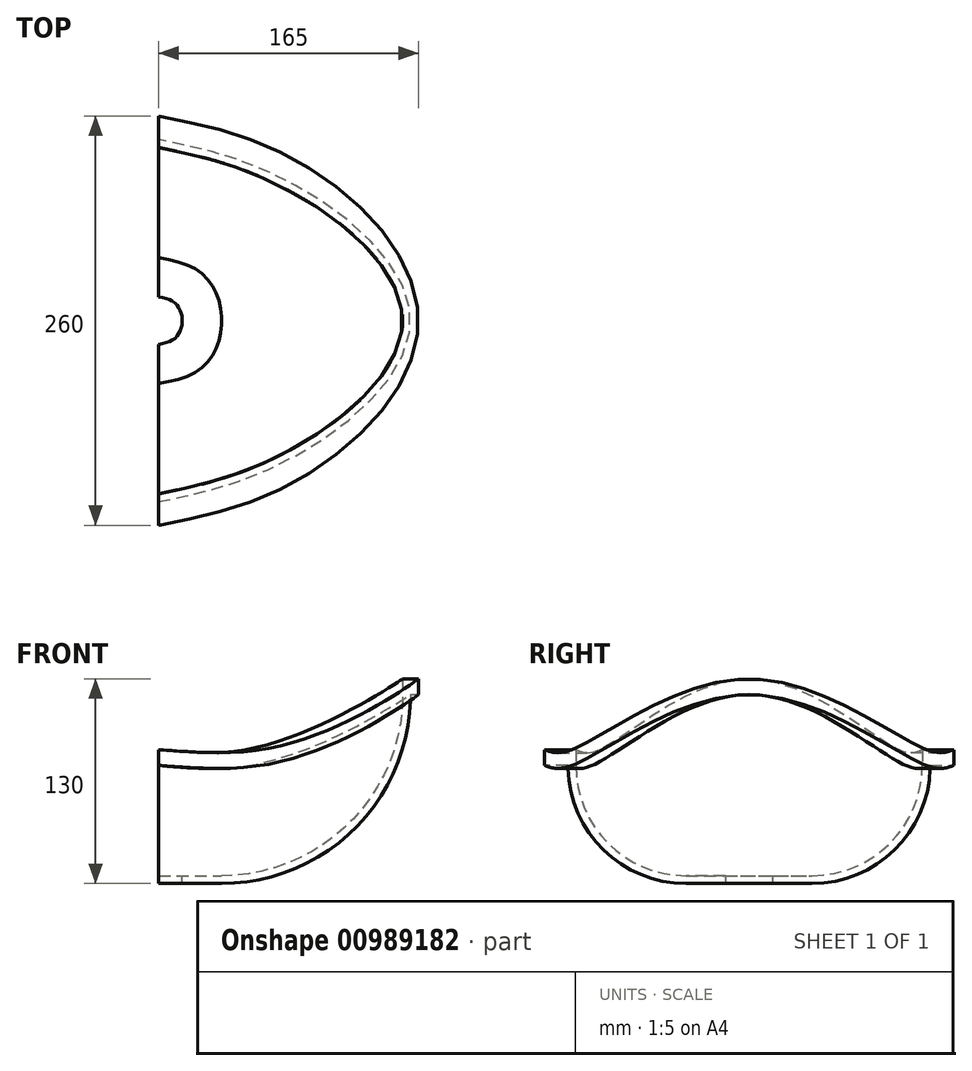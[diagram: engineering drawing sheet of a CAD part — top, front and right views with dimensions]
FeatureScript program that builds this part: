
annotation { "Feature Type Name" : "Feature", "Feature Type Description" : "" }
export const myFeature = defineFeature(function(context is Context, id is Id, definition is map)
    precondition{}
    {
        {
            var Q0;
            Q0=qCreatedBy(makeId("Front.planeOp"),FACE);
            var sketch = newSketch(context, id + "F0", { "sketchPlane" : qUnion([Q0])});
            skLineSegment(sketch, "E0.bottom", {"start": v(15, 5) * mm, "end": v(40, 5) * mm});
            skLineSegment(sketch, "E0.top", {"start": v(15, 0) * mm, "end": v(40, 0) * mm});
            skLineSegment(sketch, "E0.left", {"start": v(15, 5) * mm, "end": v(15, 0) * mm});
            skLineSegment(sketch, "E0.right", {"start": v(40, 5) * mm, "end": v(40, 0) * mm, "construction": true});
            skLineSegment(sketch, "E1.bottom", {"start": v(155, 130) * mm, "end": v(165, 130) * mm});
            skLineSegment(sketch, "E1.top", {"start": v(155, 120) * mm, "end": v(165, 120) * mm});
            skLineSegment(sketch, "E1.left", {"start": v(155, 130) * mm, "end": v(155, 120) * mm});
            skLineSegment(sketch, "E1.right", {"start": v(165, 130) * mm, "end": v(165, 120) * mm});
            skArc(sketch, "E2", {"start": v(40, 0) * mm, "mid": v(124.85, 35.15) * mm, "end": v(160, 120) * mm});
            skArc(sketch, "E3", {"start": v(40, 5) * mm, "mid": v(121.32, 38.68) * mm, "end": v(155, 120) * mm});
            skLineSegment(sketch, "E4", {"start": v(0, 0) * mm, "end": v(0, 10.01) * mm});
            skLineSegment(sketch, "E5", {"start": v(0, 0) * mm, "end": v(0, 50) * mm, "construction": true});
            skSolve(sketch);
        }
        {
            var Q0;
            Q0=sQuery(id+"F0.wireOp",EDGE,"E5");
            cPlane(context, id + "F1", {"entities" : qUnion([Q0]), "cplaneType" : CPlaneType.LINE_ANGLE, "offset" : 25 * mm, "angle" : 30 * degree, "oppositeDirection" : true, "width" : 150 * mm, "height" : 150 * mm});
        }
        {
            var Q0;
            Q0=qCreatedBy(id+"F1.planeOp",FACE);
            var sketch = newSketch(context, id + "F2", { "sketchPlane" : qUnion([Q0])});
            skLineSegment(sketch, "E6.bottom", {"start": v(15, 5) * mm, "end": v(40, 5) * mm});
            skLineSegment(sketch, "E6.top", {"start": v(15, 0) * mm, "end": v(40, 0) * mm});
            skLineSegment(sketch, "E6.left", {"start": v(15, 5) * mm, "end": v(15, 0) * mm});
            skLineSegment(sketch, "E6.right", {"start": v(40, 5) * mm, "end": v(40, 0) * mm, "construction": true});
            skLineSegment(sketch, "E7.bottom", {"start": v(110, 85) * mm, "end": v(130, 85) * mm});
            skLineSegment(sketch, "E7.top", {"start": v(110, 75) * mm, "end": v(130, 75) * mm});
            skLineSegment(sketch, "E7.left", {"start": v(110, 85) * mm, "end": v(110, 75) * mm});
            skLineSegment(sketch, "E7.right", {"start": v(130, 85) * mm, "end": v(130, 75) * mm});
            skArc(sketch, "E8", {"start": v(40, 0) * mm, "mid": v(93.03, 21.97) * mm, "end": v(115, 75) * mm});
            skArc(sketch, "E9", {"start": v(40, 5) * mm, "mid": v(89.5, 25.5) * mm, "end": v(110, 75) * mm});
            skLineSegment(sketch, "E10", {"start": v(0, 0) * mm, "end": v(0, 10.01) * mm});
            skLineSegment(sketch, "E11", {"start": v(0, 0) * mm, "end": v(0, 50) * mm, "construction": true});
            skSolve(sketch);
        }
        {
            var Q0;
            Q0=sQuery(id+"F0.wireOp",EDGE,"E5");
            cPlane(context, id + "F3", {"entities" : qUnion([Q0]), "cplaneType" : CPlaneType.LINE_ANGLE, "offset" : 25 * mm, "angle" : 150 * degree, "oppositeDirection" : true, "width" : 150 * mm, "height" : 150 * mm});
        }
        {
            var Q0;
            Q0=qCreatedBy(id+"F3.planeOp",FACE);
            var sketch = newSketch(context, id + "F4", { "sketchPlane" : qUnion([Q0])});
            skLineSegment(sketch, "E12.bottom", {"start": v(15, 5) * mm, "end": v(40, 5) * mm});
            skLineSegment(sketch, "E12.top", {"start": v(15, 0) * mm, "end": v(40, 0) * mm});
            skLineSegment(sketch, "E12.left", {"start": v(15, 5) * mm, "end": v(15, 0) * mm});
            skLineSegment(sketch, "E12.right", {"start": v(40, 5) * mm, "end": v(40, 0) * mm, "construction": true});
            skLineSegment(sketch, "E13.bottom", {"start": v(110, 85) * mm, "end": v(130, 85) * mm});
            skLineSegment(sketch, "E13.top", {"start": v(110, 75) * mm, "end": v(130, 75) * mm});
            skLineSegment(sketch, "E13.left", {"start": v(110, 85) * mm, "end": v(110, 75) * mm});
            skLineSegment(sketch, "E13.right", {"start": v(130, 85) * mm, "end": v(130, 75) * mm});
            skArc(sketch, "E14", {"start": v(40, 0) * mm, "mid": v(93.03, 21.97) * mm, "end": v(115, 75) * mm});
            skArc(sketch, "E15", {"start": v(40, 5) * mm, "mid": v(89.5, 25.5) * mm, "end": v(110, 75) * mm});
            skLineSegment(sketch, "E16", {"start": v(0, 0) * mm, "end": v(0, 10.01) * mm});
            skLineSegment(sketch, "E17", {"start": v(0, 0) * mm, "end": v(0, 50) * mm, "construction": true});
            skSolve(sketch);
        }
        {
            var Q0;
            Q0=qCreatedBy(makeId("Right.planeOp"),FACE);
            var sketch = newSketch(context, id + "F5", { "sketchPlane" : qUnion([Q0])});
            skLineSegment(sketch, "E18.bottom", {"start": v(15, 5) * mm, "end": v(40, 5) * mm});
            skLineSegment(sketch, "E18.top", {"start": v(15, 0) * mm, "end": v(40, 0) * mm});
            skLineSegment(sketch, "E18.left", {"start": v(15, 5) * mm, "end": v(15, 0) * mm});
            skLineSegment(sketch, "E18.right", {"start": v(40, 5) * mm, "end": v(40, 0) * mm, "construction": true});
            skLineSegment(sketch, "E19.bottom", {"start": v(110, 85) * mm, "end": v(130, 85) * mm});
            skLineSegment(sketch, "E19.top", {"start": v(110, 75) * mm, "end": v(130, 75) * mm});
            skLineSegment(sketch, "E19.left", {"start": v(110, 85) * mm, "end": v(110, 75) * mm});
            skLineSegment(sketch, "E19.right", {"start": v(130, 85) * mm, "end": v(130, 75) * mm});
            skArc(sketch, "E20", {"start": v(40, 0) * mm, "mid": v(93.03, 21.97) * mm, "end": v(115, 75) * mm});
            skArc(sketch, "E21", {"start": v(40, 5) * mm, "mid": v(89.5, 25.5) * mm, "end": v(110, 75) * mm});
            skLineSegment(sketch, "E22", {"start": v(0, 0) * mm, "end": v(0, 10.01) * mm});
            skLineSegment(sketch, "E23", {"start": v(0, 0) * mm, "end": v(0, 50) * mm, "construction": true});
            skSolve(sketch);
        }
        {
            var Q0;
            Q0=sQuery(id+"F5.wireOp",EDGE,"E23");
            cPlane(context, id + "F6", {"entities" : qUnion([Q0]), "cplaneType" : CPlaneType.LINE_ANGLE, "offset" : 25 * mm, "angle" : 180 * degree, "width" : 150 * mm, "height" : 150 * mm});
        }
        {
            var Q0;
            Q0=qCreatedBy(id+"F6.planeOp",FACE);
            var sketch = newSketch(context, id + "F7", { "sketchPlane" : qUnion([Q0])});
            skLineSegment(sketch, "E24.bottom", {"start": v(15, 5) * mm, "end": v(40, 5) * mm});
            skLineSegment(sketch, "E24.top", {"start": v(15, 0) * mm, "end": v(40, 0) * mm});
            skLineSegment(sketch, "E24.left", {"start": v(15, 5) * mm, "end": v(15, 0) * mm});
            skLineSegment(sketch, "E24.right", {"start": v(40, 5) * mm, "end": v(40, 0) * mm, "construction": true});
            skLineSegment(sketch, "E25.bottom", {"start": v(110, 85) * mm, "end": v(130, 85) * mm});
            skLineSegment(sketch, "E25.top", {"start": v(110, 75) * mm, "end": v(130, 75) * mm});
            skLineSegment(sketch, "E25.left", {"start": v(110, 85) * mm, "end": v(110, 75) * mm});
            skLineSegment(sketch, "E25.right", {"start": v(130, 85) * mm, "end": v(130, 75) * mm});
            skArc(sketch, "E26", {"start": v(40, 0) * mm, "mid": v(93.03, 21.97) * mm, "end": v(115, 75) * mm});
            skArc(sketch, "E27", {"start": v(40, 5) * mm, "mid": v(89.5, 25.5) * mm, "end": v(110, 75) * mm});
            skLineSegment(sketch, "E28", {"start": v(0, 0) * mm, "end": v(0, 10.01) * mm});
            skLineSegment(sketch, "E29", {"start": v(0, 0) * mm, "end": v(0, 50) * mm, "construction": true});
            skSolve(sketch);
        }
        {
            var Q0;
            Q0 = qSketchRegion(id + "F7", true);
            var Q1;
            Q1 = qSketchRegion(id + "F4", true);
            var Q2;
            Q2 = qSketchRegion(id + "F0", true);
            var Q3;
            Q3 = qSketchRegion(id + "F2", true);
            var Q4;
            Q4 = qSketchRegion(id + "F5", true);
            loft(context, id + "F8", {"sheetProfilesArray" : [{ "sheetProfileEntities" : qUnion([Q0]) }, { "sheetProfileEntities" : qUnion([Q1]) }, { "sheetProfileEntities" : qUnion([Q2]) }, { "sheetProfileEntities" : qUnion([Q3]) }, { "sheetProfileEntities" : qUnion([Q4]) }]});
        }
    });
